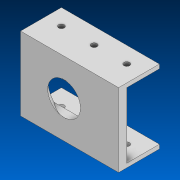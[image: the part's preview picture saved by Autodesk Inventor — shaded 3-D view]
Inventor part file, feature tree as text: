
AUTODESK INVENTOR PART (.ipt)
format: ipt  version: 2022.2 (Build 262287000, 287)  size: 143,872 bytes
history: native  units: in
note: dims shown in document units (in); Inventor stores cm internally (conversion verified against a paired STEP export)
features: sketch x4, extrude x3, chamfer x1, hole x1
ambient origin geometry x8: Origin, YZ Plane, XZ Plane, XY Plane, X Axis, Y Axis, Z Axis, Center Point
bodies: Solid1 (feature_tree)
feature tree (9):
  extrude  "Extrusion1"  Depth=1.0in
  chamfer  "Chamfer1"  Distance=1.0in
  extrude  "Extrusion2"  Depth=1.0in
  hole  "Hole1"  [1 undecoded]
  extrude  "Extrusion3"  Depth=1.0in TaperAngle=45.0deg
  sketch  "Sketch1"  dims[d0=1.0in d1=2.0in]
  sketch  "Sketch2"  dims[d3=0.168in]
  sketch  "Sketch3"  dims[d6=1.5in]
  sketch  "Sketch4"  dims[d7=1.5in d8=1.0in d9=1.0in d10=0.25in d11=0.0in d12=0.25in d13=0.25in d14=45.0deg d15=0.125in d16=1.0in d17=0.25in d18=0.0in d19=0.5in d20=1.0in d21=1.0in d22=0.5in d23=0.175in d24=0.75in d25=0.375in d26=0.25in d27=0.5635in d28=1.0in d29=0.8108in d30=1.0in d31=0.0in]
note: 1 required parameter value undecoded (feature->parameter linkage not recoverable at this tier; creation-order binding heuristic only, values carry confidence <= 0.55)
